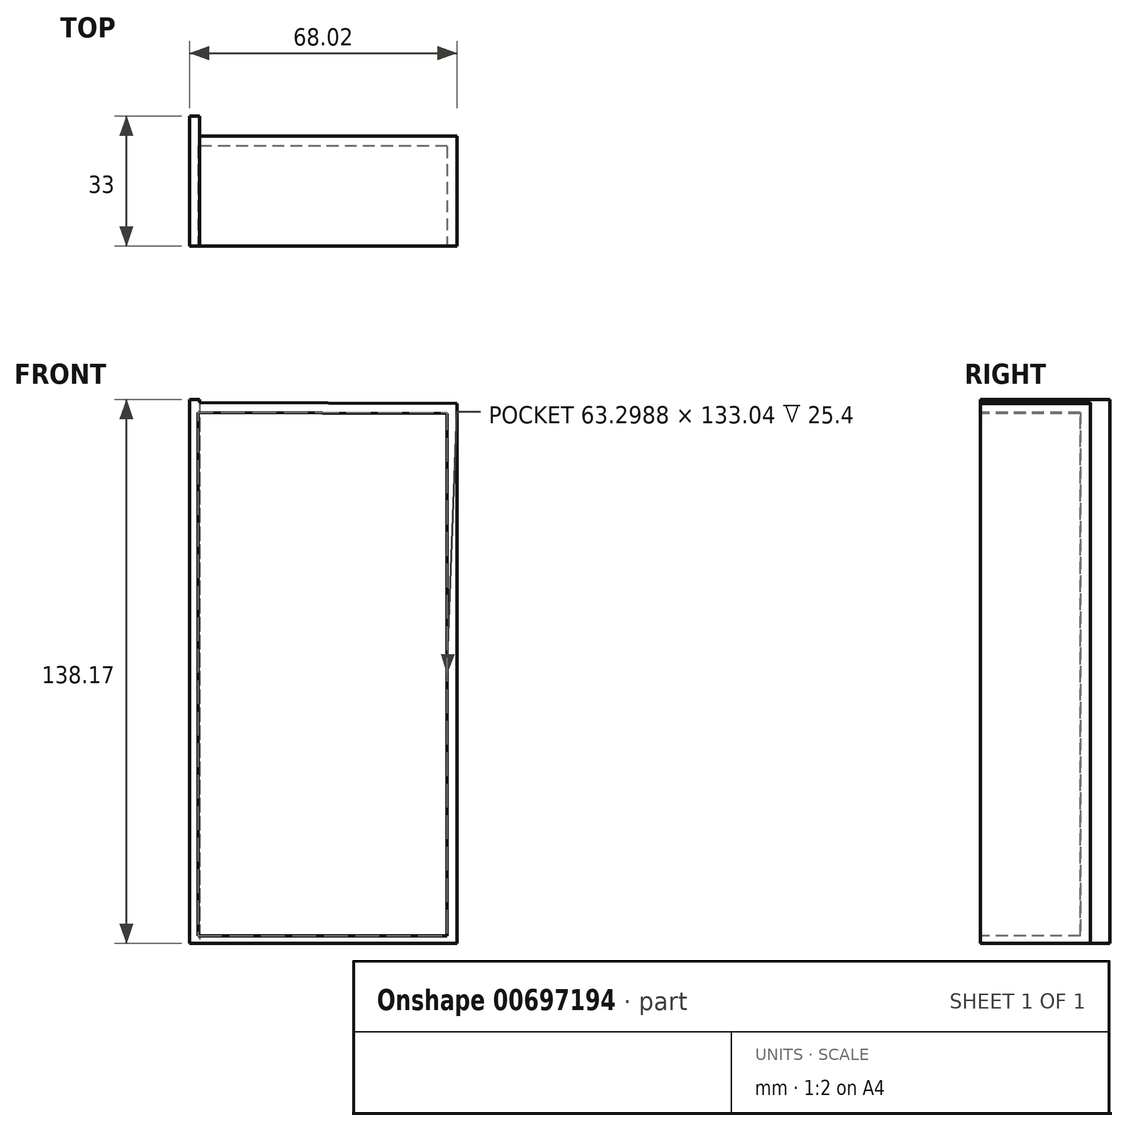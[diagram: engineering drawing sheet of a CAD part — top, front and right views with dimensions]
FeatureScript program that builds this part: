
annotation { "Feature Type Name" : "Feature", "Feature Type Description" : "" }
export const myFeature = defineFeature(function(context is Context, id is Id, definition is map)
    precondition{}
    {
        {
            var Q0;
            Q0=qCreatedBy(makeId("Front.planeOp"),FACE);
            var sketch = newSketch(context, id + "F0", { "sketchPlane" : qUnion([Q0])});
            skLineSegment(sketch, "E0", {"start": v(-53.83, 63.6) * mm, "end": v(-53.83, -74.57) * mm});
            skLineSegment(sketch, "E1", {"start": v(-53.83, -74.57) * mm, "end": v(13.22, -74.57) * mm});
            skLineSegment(sketch, "E2", {"start": v(13.22, -74.57) * mm, "end": v(13.22, 63.6) * mm});
            skLineSegment(sketch, "E3", {"start": v(13.22, 63.6) * mm, "end": v(-53.83, 63.6) * mm});
            skSolve(sketch);
        }
        {
            var Q0;
            Q0 = qSketchRegion(id + "F0", true);
            extrude(context, id + "F1", {"entities" : qUnion([Q0]), "depth" : 7.6 * mm, "offsetDistance" : 25.4 * mm});
        }
        {
            var Q0;
            Q0=makeQuery(id+"F1.opExtrude","CAP_FACE",FACE,{"disambiguationData":[OSD([sQuery(id+"F0.wireOp",EDGE,"E0"),sQuery(id+"F0.wireOp",EDGE,"E1"),sQuery(id+"F0.wireOp",EDGE,"E2"),sQuery(id+"F0.wireOp",EDGE,"E3")])],"isStart":false});
            extrude(context, id + "F2", {"entities" : qUnion([Q0]), "operationType" : NewBodyOperationType.ADD, "depth" : 25.4 * mm, "offsetDistance" : 25.4 * mm});
        }
        {
            var Q0;
            Q0=makeQuery(id+"F2.opExtrude","CAP_FACE",FACE,{"disambiguationData":[OSD([sQuery(id+"F0.wireOp",EDGE,"E0"),sQuery(id+"F0.wireOp",EDGE,"E1"),sQuery(id+"F0.wireOp",EDGE,"E2"),sQuery(id+"F0.wireOp",EDGE,"E3")])],"isStart":false});
            var sketch = newSketch(context, id + "F3", { "sketchPlane" : qUnion([Q0])});
            skLineSegment(sketch, "E4", {"start": v(-51.65, 60.36) * mm, "end": v(-51.65, -72.68) * mm});
            skLineSegment(sketch, "E5", {"start": v(-51.65, -72.68) * mm, "end": v(10, -72.68) * mm});
            skLineSegment(sketch, "E6", {"start": v(10, -72.68) * mm, "end": v(11.65, -72.68) * mm});
            skLineSegment(sketch, "E7", {"start": v(11.65, -72.68) * mm, "end": v(11.65, 60.05) * mm});
            skLineSegment(sketch, "E8", {"start": v(11.65, 60.05) * mm, "end": v(-51.65, 60.36) * mm});
            skSolve(sketch);
        }
        {
            var Q0;
            Q0 = qSketchRegion(id + "F3", true);
            extrude(context, id + "F4", {"entities" : qUnion([Q0]), "operationType" : NewBodyOperationType.REMOVE, "oppositeDirection" : true, "depth" : 25.4 * mm, "offsetDistance" : 25.4 * mm});
        }
        {
            var Q0;
            {var subQ0=sQuery(id+"F0.wireOp",EDGE,"E2");Q0=makeQuery(id+"F2.boolean.opBoolean","MERGE",FACE,{"derivedFrom":[makeQuery(id+"F1.opExtrude","SWEPT_FACE",FACE,{"disambiguationData":[OSD([subQ0])]}),makeQuery(id+"F2.opExtrude","SWEPT_FACE",FACE,{"disambiguationData":[OSD([subQ0])]})]});}
            extrude(context, id + "F5", {"entities" : qUnion([Q0]), "operationType" : NewBodyOperationType.ADD, "depth" : 25.4 * mm, "offsetDistance" : 25.4 * mm});
        }
        {
            var Q0;
            {var subQ0=sQuery(id+"F0.wireOp",EDGE,"E3");Q0=makeQuery(id+"F5.boolean.opBoolean","MERGE",FACE,{"derivedFrom":[makeQuery(id+"F2.boolean.opBoolean","MERGE",FACE,{"derivedFrom":[makeQuery(id+"F1.opExtrude","SWEPT_FACE",FACE,{"disambiguationData":[OSD([subQ0])]}),makeQuery(id+"F2.opExtrude","SWEPT_FACE",FACE,{"disambiguationData":[OSD([subQ0])]})]}),makeQuery(id+"F5.opExtrude","SWEPT_FACE",FACE,{"disambiguationData":[OSD([sQuery(id+"F0.wireOp",EDGE,"E2"),subQ0])]})]});}
            var Q1;
            Q1=makeQuery(id+"F5.opExtrude","CAP_FACE",FACE,{"disambiguationData":[OSD([sQuery(id+"F0.wireOp",EDGE,"E2")])],"isStart":false});
            var Q2;
            {var subQ0=sQuery(id+"F0.wireOp",EDGE,"E2");Q2=makeQuery(id+"F5.boolean.opBoolean","MERGE",FACE,{"derivedFrom":[makeQuery(id+"F2.opExtrude","CAP_FACE",FACE,{"disambiguationData":[OSD([sQuery(id+"F0.wireOp",EDGE,"E0"),sQuery(id+"F0.wireOp",EDGE,"E1"),subQ0,sQuery(id+"F0.wireOp",EDGE,"E3")])],"isStart":false}),makeQuery(id+"F5.opExtrude","SWEPT_FACE",FACE,{"disambiguationData":[OSD([subQ0]),TDD([makeQuery(id+"F2.opExtrude","CAP_EDGE",EDGE,{"disambiguationData":[OSD([subQ0])],"isStart":false})])]})]});}
            var Q3;
            {var subQ0=sQuery(id+"F0.wireOp",EDGE,"E1");Q3=makeQuery(id+"F5.boolean.opBoolean","MERGE",FACE,{"derivedFrom":[makeQuery(id+"F2.boolean.opBoolean","MERGE",FACE,{"derivedFrom":[makeQuery(id+"F1.opExtrude","SWEPT_FACE",FACE,{"disambiguationData":[OSD([subQ0])]}),makeQuery(id+"F2.opExtrude","SWEPT_FACE",FACE,{"disambiguationData":[OSD([subQ0])]})]}),makeQuery(id+"F5.opExtrude","SWEPT_FACE",FACE,{"disambiguationData":[OSD([subQ0,sQuery(id+"F0.wireOp",EDGE,"E2")])]})]});}
            var Q4;
            {var subQ0=sQuery(id+"F0.wireOp",EDGE,"E2");Q4=makeQuery(id+"F5.boolean.opBoolean","MERGE",FACE,{"derivedFrom":[makeQuery(id+"F1.opExtrude","CAP_FACE",FACE,{"disambiguationData":[OSD([sQuery(id+"F0.wireOp",EDGE,"E0"),sQuery(id+"F0.wireOp",EDGE,"E1"),subQ0,sQuery(id+"F0.wireOp",EDGE,"E3")])],"isStart":true}),makeQuery(id+"F5.opExtrude","SWEPT_FACE",FACE,{"disambiguationData":[OSD([subQ0]),TDD([makeQuery(id+"F1.opExtrude","CAP_EDGE",EDGE,{"disambiguationData":[OSD([subQ0])],"isStart":true})])]})]});}
            shell(context, id + "F6", {"entities" : qUnion([Q0, Q1, Q2, Q3, Q4]), "thickness" : 2.54 * mm});
        }
    });
